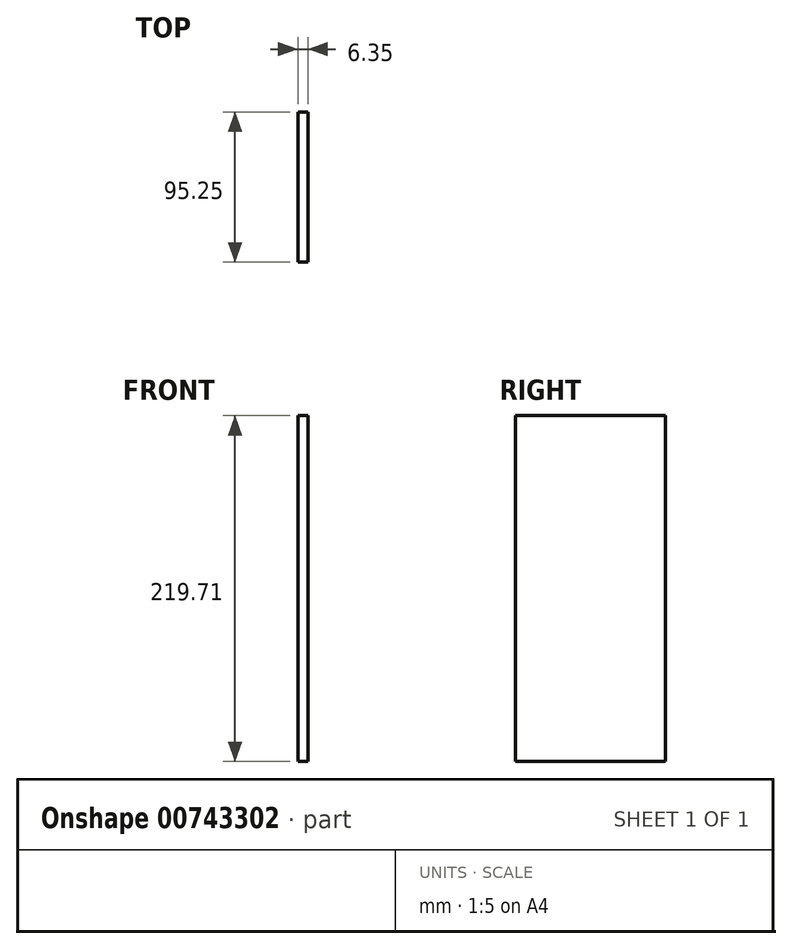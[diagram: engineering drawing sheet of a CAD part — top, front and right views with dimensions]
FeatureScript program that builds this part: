
annotation { "Feature Type Name" : "Feature", "Feature Type Description" : "" }
export const myFeature = defineFeature(function(context is Context, id is Id, definition is map)
    precondition{}
    {
        {
            var Q0;
            Q0=qCreatedBy(makeId("Right.planeOp"),FACE);
            var sketch = newSketch(context, id + "F0", { "sketchPlane" : qUnion([Q0])});
            skLineSegment(sketch, "E0.bottom", {"start": v(-36.4, 133.23) * mm, "end": v(58.85, 133.23) * mm});
            skLineSegment(sketch, "E0.top", {"start": v(-36.4, -86.48) * mm, "end": v(58.85, -86.48) * mm});
            skLineSegment(sketch, "E0.left", {"start": v(-36.4, 133.23) * mm, "end": v(-36.4, -86.48) * mm});
            skLineSegment(sketch, "E0.right", {"start": v(58.85, 133.23) * mm, "end": v(58.85, -86.48) * mm});
            skSolve(sketch);
        }
        {
            var Q0;
            Q0=makeQuery(id+"F0.imprint","IMPRINT",FACE,{"disambiguationData":[TD([[makeQuery(id+"F0.imprint","IMPRINT",EDGE,{"derivedFrom":sQuery(id+"F0.wireOp",EDGE,"E0.bottom")}),-1.0]])]});
            extrude(context, id + "F1", {"entities" : qUnion([Q0]), "depth" : 6.35 * mm, "offsetDistance" : 25.4 * mm});
        }
    });
